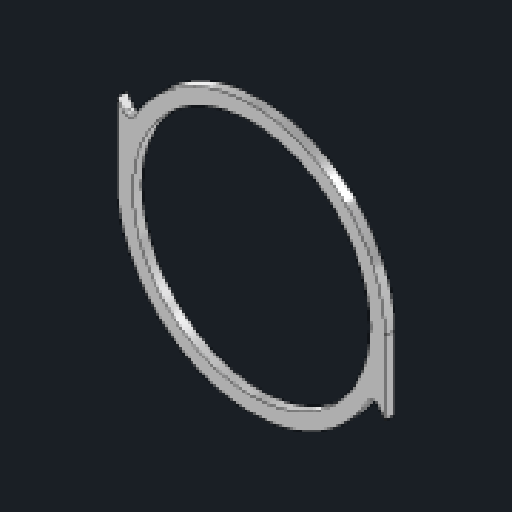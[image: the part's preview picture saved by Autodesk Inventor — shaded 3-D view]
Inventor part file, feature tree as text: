
AUTODESK INVENTOR PART (.ipt)
format: ipt  version: 2023.2 (Build 272271030, 271C)  size: 119,808 bytes
history: native  units: mm
features: extrude x1, sketch x1
ambient origin geometry x8: Origin, YZ Plane, XZ Plane, XY Plane, X Axis, Y Axis, Z Axis, Center Point
bodies: Solid1 (feature_tree)
feature tree (2):
  extrude  "Extrusion1"  Depth=3.1mm
  sketch  "Sketch1"  dims[d0=127.0mm d1=8.0mm d2=5.0mm d3=0.0mm d4=10.0mm d5=3.1mm d6=20.0mm d8=360.0deg]
